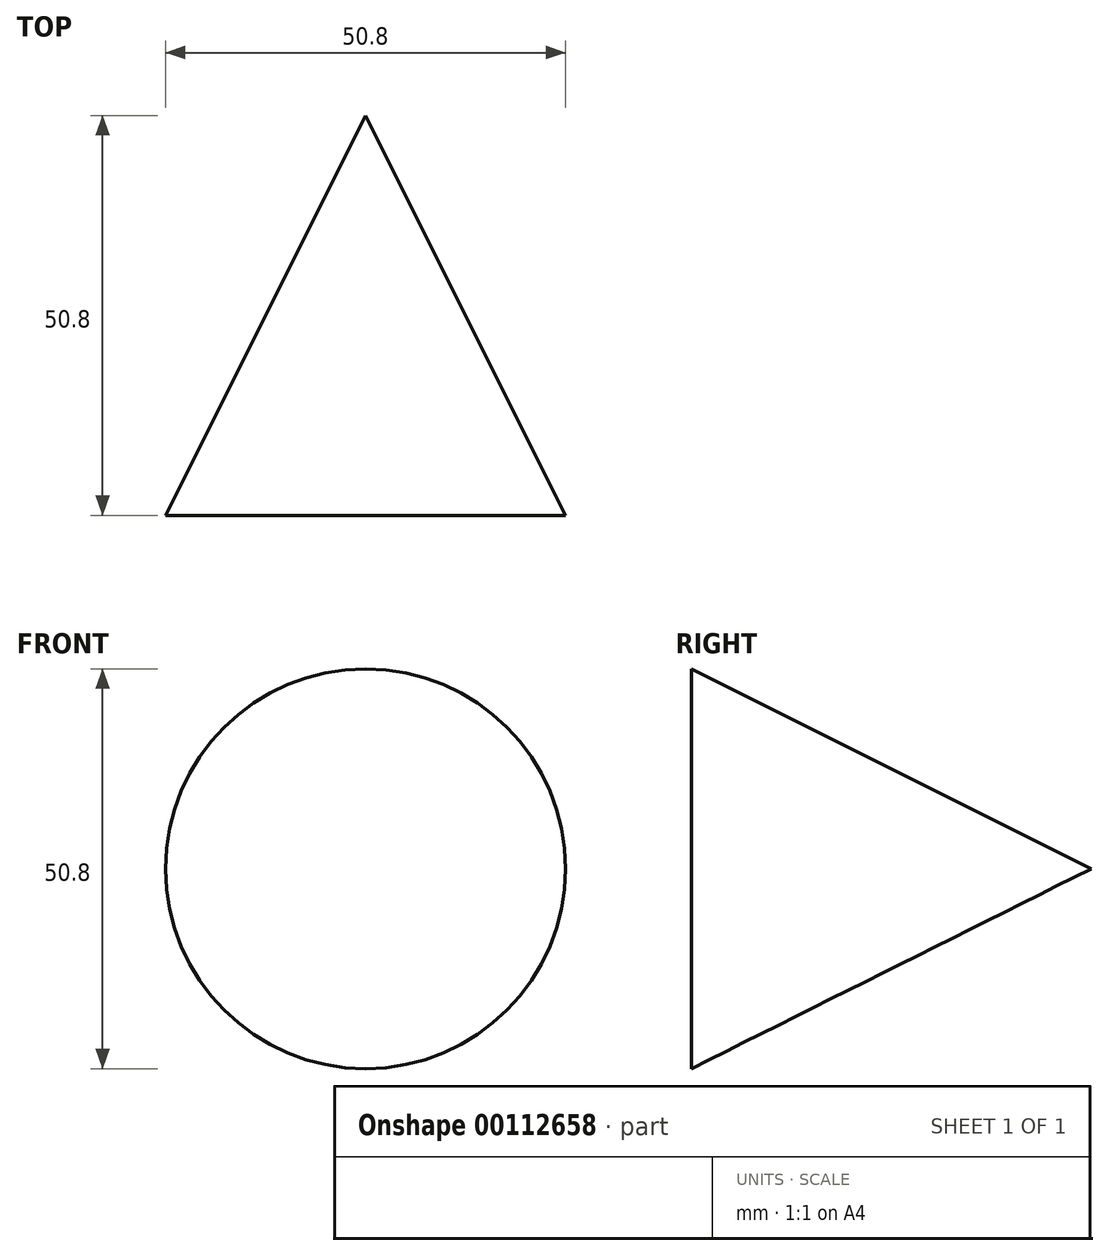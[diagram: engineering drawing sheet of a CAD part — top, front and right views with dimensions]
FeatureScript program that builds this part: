
annotation { "Feature Type Name" : "Feature", "Feature Type Description" : "" }
export const myFeature = defineFeature(function(context is Context, id is Id, definition is map)
    precondition{}
    {
        {
            var Q0;
            Q0=qCreatedBy(makeId("Top.planeOp"),FACE);
            var sketch = newSketch(context, id + "F0", { "sketchPlane" : qUnion([Q0])});
            skLineSegment(sketch, "E0", {"start": v(0, 0) * mm, "end": v(0, 50.8) * mm});
            skLineSegment(sketch, "E1", {"start": v(0, 50.8) * mm, "end": v(25.4, 0) * mm});
            skLineSegment(sketch, "E2", {"start": v(0, 0) * mm, "end": v(25.4, 0) * mm});
            skSolve(sketch);
        }
        {
            var Q0;
            Q0=qCreatedBy(makeId("Front.planeOp"),FACE);
            var sketch = newSketch(context, id + "F1", { "sketchPlane" : qUnion([Q0])});
            skCircle(sketch, "E3", {"center": v(0, 0) * mm, "radius": 25.4 * mm});
            skSolve(sketch);
        }
        {
            var Q0;
            Q0=makeQuery(id+"F0.imprint","IMPRINT",FACE,{"disambiguationData":[TD([[makeQuery(id+"F0.imprint","IMPRINT",EDGE,{"derivedFrom":sQuery(id+"F0.wireOp",EDGE,"E0")}),-1.0]])]});
            var Q1;
            Q1=sQuery(id+"F1.wireOp",EDGE,"E3");
            revolve(context, id + "F2", {"entities" : qUnion([Q0]), "axis" : qUnion([Q1]), "revolveType" : RevolveType.FULL});
        }
    });
